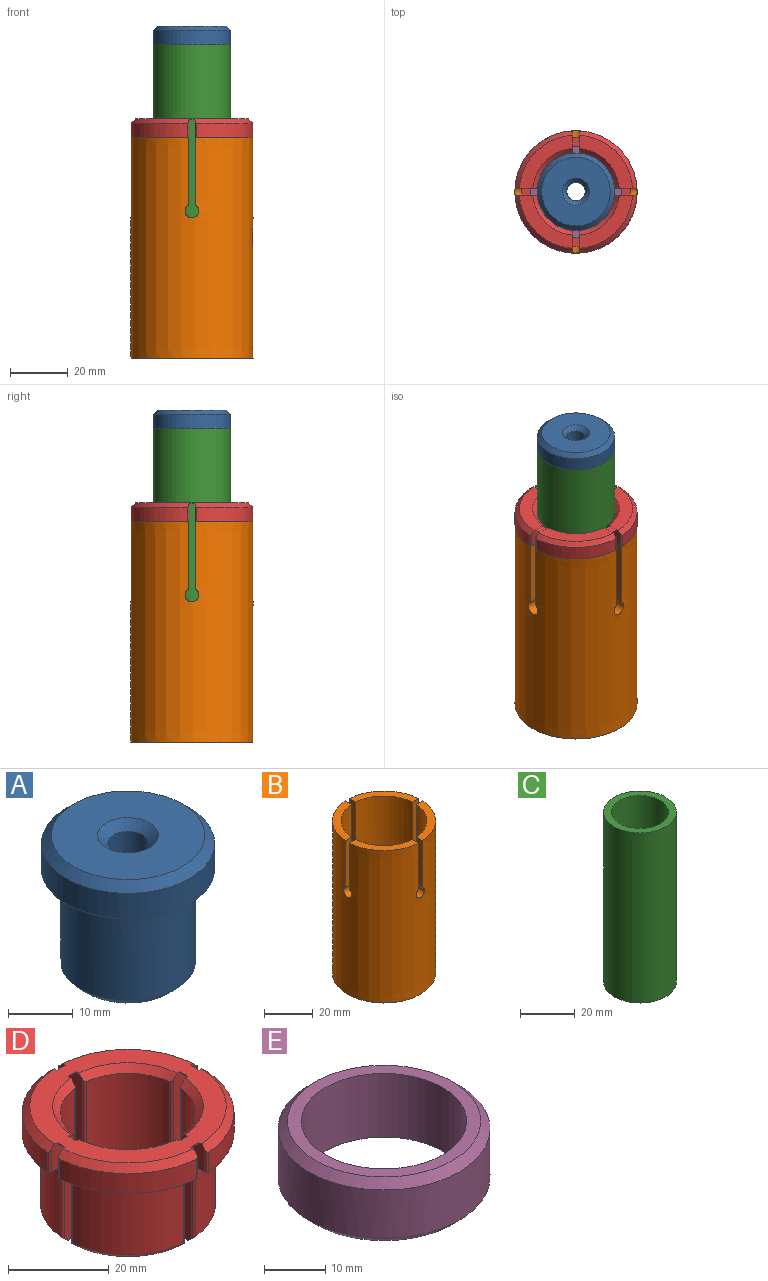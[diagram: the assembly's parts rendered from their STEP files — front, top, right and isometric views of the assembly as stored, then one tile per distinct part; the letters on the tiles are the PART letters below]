
ASSEMBLY  parts=5 mates=4
PART A: 16 faces, bbox 26.7x26.7x25.4 mm
  f0: cylinder r=3.17mm len=18.32mm, axis (0,0,1), area 365.5mm2, adj f7,f15
  f1: plane 23.62x23.62mm, normal (0,0,1), area 368.9mm2, adj f7,f8
  f2: cylinder r=13.33mm len=26.67mm, axis (0,0,1), area 404.4mm2, adj f3,f8
  f3: plane 26.67x26.67mm, normal (0,0,-1), area 222.9mm2, adj f2,f4
  f4: cylinder r=10.34mm len=20.68mm, axis (0,0,1), area 1138.4mm2, adj f3,f6
  f5: plane 17.63x17.63mm, normal (0,0,-1), area 131.9mm2, adj f6,f9,f10,f11,f12,f13,f14
  f6: cone r=10.34mm half-angle=45deg, axis (0,0,1), area 129.7mm2, adj f4,f5
  f7: cone r=3.17mm half-angle=45deg, axis (0,0,1), area 53.3mm2, adj f0,f1
  f8: cone r=11.81mm half-angle=45deg, axis (0,0,-1), area 170.3mm2, adj f1,f2
  f9: plane 6.57x5.56mm, normal (0,-1,0), area 36.5mm2, adj f5,f10,f14,f15
  f10: plane 5.69x5.56mm, normal (-0.87,-0.5,0), area 36.5mm2, adj f5,f9,f11,f15
  f11: plane 5.69x5.56mm, normal (-0.87,0.5,0), area 36.5mm2, adj f5,f10,f12,f15
  f12: plane 6.57x5.56mm, normal (0,1,0), area 36.5mm2, adj f5,f11,f13,f15
  f13: plane 5.69x5.56mm, normal (0.87,0.5,0), area 36.5mm2, adj f5,f12,f14,f15
  f14: plane 5.69x5.56mm, normal (0.87,-0.5,0), area 36.5mm2, adj f5,f9,f13,f15
  f15: plane 13.14x11.38mm, normal (0,0,-1), area 80.5mm2, adj f0,f9,f10,f11,f12,f13,f14
PART B: 22 faces, bbox 42.2x42.2x76.2 mm
  f0: plane 19.91x19.91mm, normal (0,0,1), area 99.7mm2, adj f4,f5,f6,f7,f11,f20
  f1: extruded ~76.2x42.1mm, area 7522.9mm2, adj f2,f3,f7,f8,f9,f10,f12,f13
  f2: plane 19.92x19.92mm, normal (0,0,1), area 99.7mm2, adj f1,f6,f18,f19
  f3: plane 19.92x19.92mm, normal (0,0,1), area 99.7mm2, adj f1,f6,f15,f17
  f4: extruded ~23.72x0.55mm, area 12.9mm2, adj f0,f7,f10,f11
  f5: extruded ~23.72x0.55mm, area 12.9mm2, adj f0,f7,f20,f21
  f6: cylinder r=17.53mm len=76.2mm, axis (0,0,1), area 8108.1mm2, adj f0,f2,f3,f8,f9,f10,f11,f12
  f7: cylinder r=21.08mm len=76.2mm, axis (0,0,1), area 2262.1mm2, adj f0,f1,f4,f5,f8,f10,f21
  f8: plane 42.17x42.17mm, normal (0,0,-1), area 431.4mm2, adj f1,f6,f7
  f9: plane 19.92x19.92mm, normal (0,0,1), area 99.7mm2, adj f1,f6,f12,f14
  f10: cylinder r=2.38mm len=4.76mm, axis (0,-1,0), area 44.9mm2, adj f1,f4,f6,f7,f11,f12
  f11: plane 23.31x3.56mm, normal (-1,0,0), area 83mm2, adj f0,f4,f6,f10
  f12: plane 23.31x3.56mm, normal (1,0,0), area 83mm2, adj f1,f6,f9,f10
  f13: cylinder r=2.38mm len=4.76mm, axis (1,0,0), area 44.9mm2, adj f1,f6,f14,f15
  f14: plane 23.31x3.56mm, normal (0,-1,0), area 83mm2, adj f1,f6,f9,f13
  f15: plane 23.31x3.56mm, normal (0,1,0), area 83mm2, adj f1,f3,f6,f13
  f16: cylinder r=2.38mm len=4.76mm, axis (0,1,0), area 44.9mm2, adj f1,f6,f17,f18
  f17: plane 23.31x3.56mm, normal (1,0,0), area 83mm2, adj f1,f3,f6,f16
  f18: plane 23.31x3.56mm, normal (-1,0,0), area 83mm2, adj f1,f2,f6,f16
  f19: plane 23.31x3.56mm, normal (0,1,0), area 83mm2, adj f1,f2,f6,f21
  f20: plane 23.31x3.56mm, normal (0,-1,0), area 83mm2, adj f0,f5,f6,f21
  f21: cylinder r=2.38mm len=4.76mm, axis (-1,0,0), area 44.9mm2, adj f1,f5,f6,f7,f19,f20
PART C: 4 faces, bbox 26.7x26.7x76.2 mm
  f0: cylinder r=10.46mm len=76.2mm, axis (0,0,1), area 5010.3mm2, adj f2,f3
  f1: cylinder r=13.33mm len=76.2mm, axis (0,0,1), area 6384.5mm2, adj f2,f3
  f2: plane 26.67x26.67mm, normal (0,0,-1), area 214.6mm2, adj f0,f1
  f3: plane 26.67x26.67mm, normal (0,0,1), area 214.6mm2, adj f0,f1
PART D: 81 faces, bbox 42.1x42.1x25.4 mm
  f0: cylinder r=13.46mm len=22.35mm, axis (0,0,1), area 401.4mm2, adj f6,f9,f71,f80
  f1: plane 39.05x39.05mm, normal (0,0,1), area 482.2mm2, adj f8,f9,f10,f11,f12,f13,f15,f21
  f2: cylinder r=21.08mm len=19.32mm, axis (0,0,1), area 143.5mm2, adj f3,f8,f69,f78
  f3: plane 19.87x19.87mm, normal (0,0,-1), area 102.9mm2, adj f2,f4,f10,f11,f69,f70,f78,f79
  f4: cylinder r=17.4mm len=17.53mm, axis (0,0,1), area 419.3mm2, adj f3,f7,f70,f79
  f5: plane 14.69x14.69mm, normal (0,0,-1), area 19.5mm2, adj f6,f7,f10,f11
  f6: cone r=14.99mm half-angle=45deg, axis (0,0,-1), area 43.1mm2, adj f0,f5,f10,f11,f71,f80
  f7: cone r=17.4mm half-angle=45deg, axis (0,0,1), area 51.2mm2, adj f4,f5,f10,f11,f70,f79
  f8: cone r=19.56mm half-angle=45deg, axis (0,0,-1), area 63.7mm2, adj f1,f2,f10,f11,f69,f78
  f9: cone r=13.46mm half-angle=45deg, axis (0,0,1), area 43.1mm2, adj f0,f1,f10,f11,f71,f80
  f10: plane 25.4x6.64mm, normal (0,1,0), area 95.2mm2, adj f1,f3,f5,f6,f7,f8,f9,f12
  f11: plane 25.4x6.64mm, normal (-1,0,0), area 95.2mm2, adj f1,f3,f5,f6,f7,f8,f9,f26
  f12: cylinder r=18.8mm len=2.29mm, axis (0,0,1), area 0.6mm2, adj f1,f10,f14,f30
  f13: cylinder r=15.75mm len=2.29mm, axis (0,0,1), area 0.6mm2, adj f1,f10,f14,f30
  f14: plane 3.09x2.29mm, normal (0,0,-1), area 7mm2, adj f10,f12,f13,f30
  f15: cone r=13.46mm half-angle=45deg, axis (0,0,1), area 43.1mm2, adj f1,f23,f24,f25,f65,f74
  f16: cone r=14.99mm half-angle=45deg, axis (0,0,-1), area 43.1mm2, adj f18,f23,f24,f25,f65,f74
  f17: cone r=17.4mm half-angle=45deg, axis (0,0,1), area 51.2mm2, adj f18,f19,f24,f25,f64,f73
  f18: plane 14.69x14.69mm, normal (0,0,-1), area 19.5mm2, adj f16,f17,f24,f25
  f19: cylinder r=17.4mm len=17.53mm, axis (0,0,1), area 419.3mm2, adj f17,f20,f64,f73
  f20: plane 19.87x19.87mm, normal (0,0,-1), area 102.9mm2, adj f19,f22,f24,f25,f63,f64,f72,f73
  f21: cone r=19.56mm half-angle=45deg, axis (0,0,-1), area 63.7mm2, adj f1,f22,f24,f25,f63,f72
  f22: cylinder r=21.08mm len=19.32mm, axis (0,0,1), area 143.5mm2, adj f20,f21,f63,f72
  f23: cylinder r=13.46mm len=22.35mm, axis (0,0,1), area 401.4mm2, adj f15,f16,f65,f74
  f24: plane 25.4x6.64mm, normal (1,0,0), area 95.2mm2, adj f1,f15,f16,f17,f18,f20,f21,f26
  f25: plane 25.4x6.64mm, normal (0,1,0), area 95.2mm2, adj f1,f15,f16,f17,f18,f20,f21,f54
  f26: cylinder r=18.8mm len=2.29mm, axis (0,0,1), area 0.6mm2, adj f1,f11,f24,f28
  f27: cylinder r=15.75mm len=2.29mm, axis (0,0,1), area 0.6mm2, adj f1,f11,f24,f28
  f28: plane 3.09x2.29mm, normal (0,0,-1), area 7mm2, adj f11,f24,f26,f27
  f29: plane 25.4x6.64mm, normal (-1,0,0), area 95.2mm2, adj f1,f31,f32,f33,f35,f36,f38,f51
  f30: plane 25.4x6.64mm, normal (0,-1,0), area 95.2mm2, adj f1,f12,f13,f14,f31,f32,f33,f35
  f31: cone r=13.46mm half-angle=45deg, axis (0,0,1), area 43.1mm2, adj f1,f29,f30,f39,f62,f77
  f32: cone r=14.99mm half-angle=45deg, axis (0,0,-1), area 43.1mm2, adj f29,f30,f38,f39,f62,f77
  f33: cone r=17.4mm half-angle=45deg, axis (0,0,1), area 51.2mm2, adj f29,f30,f34,f38,f61,f76
  f34: cylinder r=17.4mm len=17.53mm, axis (0,0,1), area 419.3mm2, adj f33,f35,f61,f76
  f35: plane 19.87x19.87mm, normal (0,0,-1), area 102.9mm2, adj f29,f30,f34,f37,f60,f61,f75,f76
  f36: cone r=19.56mm half-angle=45deg, axis (0,0,-1), area 63.7mm2, adj f1,f29,f30,f37,f60,f75
  f37: cylinder r=21.08mm len=19.32mm, axis (0,0,1), area 143.5mm2, adj f35,f36,f60,f75
  f38: plane 14.69x14.69mm, normal (0,0,-1), area 19.5mm2, adj f29,f30,f32,f33
  f39: cylinder r=13.46mm len=22.35mm, axis (0,0,1), area 401.4mm2, adj f31,f32,f62,f77
  f40: cylinder r=13.46mm len=22.35mm, axis (0,0,1), area 401.4mm2, adj f47,f48,f59,f68
  f41: plane 14.69x14.69mm, normal (0,0,-1), area 19.5mm2, adj f46,f47,f49,f50
  f42: cylinder r=21.08mm len=19.32mm, axis (0,0,1), area 143.5mm2, adj f43,f44,f57,f66
  f43: cone r=19.56mm half-angle=45deg, axis (0,0,-1), area 63.7mm2, adj f1,f42,f49,f50,f57,f66
  f44: plane 19.87x19.87mm, normal (0,0,-1), area 102.9mm2, adj f42,f45,f49,f50,f57,f58,f66,f67
  f45: cylinder r=17.4mm len=17.53mm, axis (0,0,1), area 419.3mm2, adj f44,f46,f58,f67
  f46: cone r=17.4mm half-angle=45deg, axis (0,0,1), area 51.2mm2, adj f41,f45,f49,f50,f58,f67
  f47: cone r=14.99mm half-angle=45deg, axis (0,0,-1), area 43.1mm2, adj f40,f41,f49,f50,f59,f68
  f48: cone r=13.46mm half-angle=45deg, axis (0,0,1), area 43.1mm2, adj f1,f40,f49,f50,f59,f68
  f49: plane 25.4x6.64mm, normal (0,-1,0), area 95.2mm2, adj f1,f41,f43,f44,f46,f47,f48,f54
  f50: plane 25.4x6.64mm, normal (1,0,0), area 95.2mm2, adj f1,f41,f43,f44,f46,f47,f48,f51
  f51: plane 3.09x2.29mm, normal (0,0,-1), area 7mm2, adj f29,f50,f52,f53
  f52: cylinder r=15.75mm len=2.29mm, axis (0,0,1), area 0.6mm2, adj f1,f29,f50,f51
  f53: cylinder r=18.8mm len=2.29mm, axis (0,0,1), area 0.6mm2, adj f1,f29,f50,f51
  f54: cylinder r=18.8mm len=2.29mm, axis (0,0,1), area 0.6mm2, adj f1,f25,f49,f56
  f55: cylinder r=15.75mm len=2.29mm, axis (0,0,1), area 0.6mm2, adj f1,f25,f49,f56
  f56: plane 3.09x2.29mm, normal (0,0,-1), area 7mm2, adj f25,f49,f54,f55
  f57: cylinder r=0.51mm len=5.37mm, axis (0,0,1), area 4.2mm2, adj f42,f43,f44,f50
  f58: cylinder r=0.51mm len=18.08mm, axis (0,0,1), area 15mm2, adj f44,f45,f46,f50
  f59: cylinder r=0.51mm len=23.27mm, axis (0,0,1), area 16.8mm2, adj f40,f47,f48,f50
  f60: cylinder r=0.51mm len=5.37mm, axis (0,0,1), area 4.2mm2, adj f29,f35,f36,f37
  f61: cylinder r=0.51mm len=18.08mm, axis (0,0,1), area 15mm2, adj f29,f33,f34,f35
  f62: cylinder r=0.51mm len=23.27mm, axis (0,0,1), area 16.8mm2, adj f29,f31,f32,f39
  f63: cylinder r=0.51mm len=5.37mm, axis (0,0,1), area 4.2mm2, adj f20,f21,f22,f25
  f64: cylinder r=0.51mm len=18.08mm, axis (0,0,1), area 15mm2, adj f17,f19,f20,f25
  f65: cylinder r=0.51mm len=23.27mm, axis (0,0,1), area 16.8mm2, adj f15,f16,f23,f25
  f66: cylinder r=0.51mm len=5.37mm, axis (0,0,1), area 4.2mm2, adj f42,f43,f44,f49
  f67: cylinder r=0.51mm len=18.08mm, axis (0,0,1), area 15mm2, adj f44,f45,f46,f49
  f68: cylinder r=0.51mm len=23.27mm, axis (0,0,1), area 16.8mm2, adj f40,f47,f48,f49
  f69: cylinder r=0.51mm len=5.37mm, axis (0,0,1), area 4.2mm2, adj f2,f3,f8,f11
  f70: cylinder r=0.51mm len=18.08mm, axis (0,0,1), area 15mm2, adj f3,f4,f7,f11
  f71: cylinder r=0.51mm len=23.27mm, axis (0,0,1), area 16.8mm2, adj f0,f6,f9,f11
  f72: cylinder r=0.51mm len=5.37mm, axis (0,0,1), area 4.2mm2, adj f20,f21,f22,f24
  f73: cylinder r=0.51mm len=18.08mm, axis (0,0,1), area 15mm2, adj f17,f19,f20,f24
  f74: cylinder r=0.51mm len=23.27mm, axis (0,0,1), area 16.8mm2, adj f15,f16,f23,f24
  f75: cylinder r=0.51mm len=5.37mm, axis (0,0,1), area 4.2mm2, adj f30,f35,f36,f37
  f76: cylinder r=0.51mm len=18.08mm, axis (0,0,1), area 15mm2, adj f30,f33,f34,f35
  f77: cylinder r=0.51mm len=23.27mm, axis (0,0,1), area 16.8mm2, adj f30,f31,f32,f39
  f78: cylinder r=0.51mm len=5.37mm, axis (0,0,1), area 4.2mm2, adj f2,f3,f8,f10
  f79: cylinder r=0.51mm len=18.08mm, axis (0,0,1), area 15mm2, adj f3,f4,f7,f10
  f80: cylinder r=0.51mm len=23.27mm, axis (0,0,1), area 16.8mm2, adj f0,f6,f9,f10
PART E: 6 faces, bbox 34.5x34.5x12.7 mm
  f0: cylinder r=13.46mm len=26.92mm, axis (0,0,1), area 1074.2mm2, adj f1,f3
  f1: plane 31.5x31.5mm, normal (0,0,1), area 209.8mm2, adj f0,f5
  f2: cylinder r=17.27mm len=34.54mm, axis (0,0,1), area 1047.5mm2, adj f4,f5
  f3: plane 31.5x31.5mm, normal (0,0,-1), area 209.8mm2, adj f0,f4
  f4: cone r=17.27mm half-angle=45deg, axis (0,0,1), area 223.6mm2, adj f2,f3
  f5: cone r=15.75mm half-angle=45deg, axis (0,0,-1), area 223.6mm2, adj f1,f2
PLACE A t=(0,0,-56.17)mm
PLACE B t=(0,0,-88.25)mm
PLACE C t=(0,0,-56.17)mm
PLACE D t=(0,0,-88.25)mm
PLACE E t=(0,0,-56.17)mm
MATE fastened A.f0 <-> C.f0  axis (0,0,1) through (0,0,-62.52)mm
MATE fastened D.f0 <-> B.f6  axis (0,0,1) through (0,0,-94.6)mm
MATE cylindrical C.f1 <-> D.f0  axis (0,0,1) through (0,0,-100.62)mm
MATE fastened E.f0 <-> C.f0  axis (0,0,1) through (0,0,-138.72)mm
